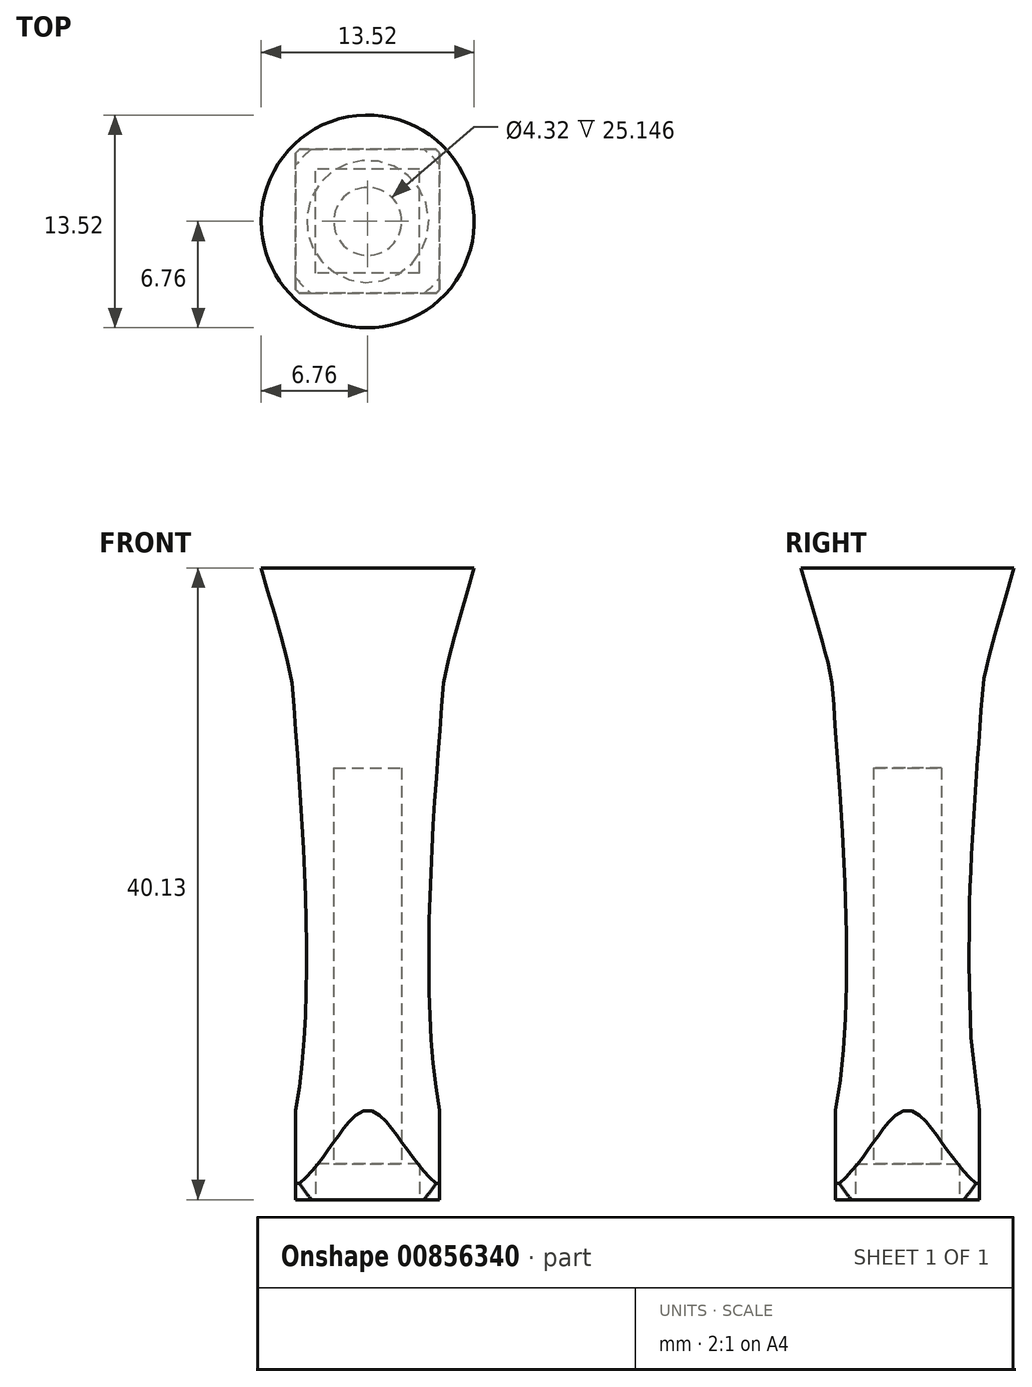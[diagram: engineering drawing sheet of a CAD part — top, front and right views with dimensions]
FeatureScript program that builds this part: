
annotation { "Feature Type Name" : "Feature", "Feature Type Description" : "" }
export const myFeature = defineFeature(function(context is Context, id is Id, definition is map)
    precondition{}
    {
        {
            var Q0;
            Q0=qCreatedBy(makeId("Front.planeOp"),FACE);
            var sketch = newSketch(context, id + "F0", { "sketchPlane" : qUnion([Q0])});
            skLineSegment(sketch, "E0", {"start": v(0, 0) * mm, "end": v(2.16, 0) * mm});
            skLineSegment(sketch, "E1", {"start": v(2.16, 0) * mm, "end": v(2.16, 25.4) * mm});
            skLineSegment(sketch, "E2", {"start": v(2.16, 25.4) * mm, "end": v(0, 25.4) * mm});
            skLineSegment(sketch, "E3", {"start": v(0, 25.4) * mm, "end": v(0, 38.1) * mm});
            skArc(sketch, "E4", {"start": v(0, 38.1) * mm, "mid": v(3.48, 38.26) * mm, "end": v(6.94, 38.74) * mm});
            skLineSegment(sketch, "E5", {"start": v(0, 0) * mm, "end": v(0, -2.03) * mm});
            skLineSegment(sketch, "E6", {"start": v(0, -2.03) * mm, "end": v(7.62, -2.03) * mm});
            skFitSpline(sketch, "E7", {"points": [v(7.62, -2.03) * mm, v(4.61, 28.24) * mm, v(6.94, 38.74) * mm], "startDerivative": vector(-26.12, 9.72) * mm, "endDerivative": vector(18.7, 66.57) * mm});
            skLineSegment(sketch, "E8", {"start": v(0, 38.1) * mm, "end": v(12.68, 38.1) * mm});
            skSolve(sketch);
        }
        {
            var Q0;
            Q0=makeQuery(id+"F0.imprint","IMPRINT",FACE,{"disambiguationData":[TD([[makeQuery(id+"F0.imprint","IMPRINT",EDGE,{"derivedFrom":sQuery(id+"F0.wireOp",EDGE,"E0")}),-1.0]])]});
            var Q1;
            Q1=sQuery(id+"F0.wireOp",EDGE,"E3");
            revolve(context, id + "F1", {"surfaceOperationType" : NewSurfaceOperationType.NEW, "entities" : qUnion([Q0]), "axis" : qUnion([Q1]), "revolveType" : RevolveType.FULL});
        }
        {
            var Q0;
            Q0=makeQuery(id+"F1.opRevolve","SWEPT_FACE",FACE,{"disambiguationData":[OSD([sQuery(id+"F0.wireOp",EDGE,"E6")])]});
            var sketch = newSketch(context, id + "F2", { "sketchPlane" : qUnion([Q0])});
            skLineSegment(sketch, "E9.bottom", {"start": v(3.3, 3.3) * mm, "end": v(-3.3, 3.3) * mm});
            skLineSegment(sketch, "E9.top", {"start": v(3.3, -3.3) * mm, "end": v(-3.3, -3.3) * mm});
            skLineSegment(sketch, "E9.left", {"start": v(3.3, 3.3) * mm, "end": v(3.3, -3.3) * mm});
            skLineSegment(sketch, "E9.right", {"start": v(-3.3, 3.3) * mm, "end": v(-3.3, -3.3) * mm});
            skPoint(sketch, "E9.middle", {"position": v(0, 0) * mm});
            skLineSegment(sketch, "E10.bottom", {"start": v(-4.57, 4.57) * mm, "end": v(4.57, 4.57) * mm});
            skLineSegment(sketch, "E10.top", {"start": v(-4.57, -4.57) * mm, "end": v(4.57, -4.57) * mm});
            skLineSegment(sketch, "E10.left", {"start": v(-4.57, 4.57) * mm, "end": v(-4.57, -4.57) * mm});
            skLineSegment(sketch, "E10.right", {"start": v(4.57, 4.57) * mm, "end": v(4.57, -4.57) * mm});
            skLineSegment(sketch, "E11.0", {"start": v(-8.26, 8.26) * mm, "end": v(8.26, 8.26) * mm});
            skLineSegment(sketch, "E11.1", {"start": v(-8.26, 8.26) * mm, "end": v(-8.26, -8.26) * mm});
            skLineSegment(sketch, "E11.2", {"start": v(-8.26, -8.26) * mm, "end": v(8.26, -8.26) * mm});
            skLineSegment(sketch, "E11.3", {"start": v(8.26, 8.26) * mm, "end": v(8.26, -8.26) * mm});
            skSolve(sketch);
        }
        {
            var Q0;
            Q0=makeQuery(id+"F2.imprint","IMPRINT",FACE,{"disambiguationData":[TD([[makeQuery(id+"F2.imprint","IMPRINT",EDGE,{"derivedFrom":sQuery(id+"F2.wireOp",EDGE,"E9.bottom")}),1.0]])]});
            extrude(context, id + "F3", {"entities" : qUnion([Q0]), "operationType" : NewBodyOperationType.REMOVE, "oppositeDirection" : true, "depth" : 2.3 * mm, "offsetDistance" : 25.4 * mm});
        }
        {
            var Q0;
            Q0=makeQuery(id+"F3.boolean.opBoolean","COPY",EDGE,{"derivedFrom":makeQuery(id+"F3.opExtrude","CAP_EDGE",EDGE,{"disambiguationData":[OSD([sQuery(id+"F2.wireOp",EDGE,"E9.left")])],"isStart":true})});
            var Q1;
            Q1=makeQuery(id+"F3.boolean.opBoolean","COPY",EDGE,{"derivedFrom":makeQuery(id+"F3.opExtrude","CAP_EDGE",EDGE,{"disambiguationData":[OSD([sQuery(id+"F2.wireOp",EDGE,"E9.bottom")])],"isStart":true})});
            var Q2;
            Q2=makeQuery(id+"F3.boolean.opBoolean","COPY",EDGE,{"derivedFrom":makeQuery(id+"F3.opExtrude","CAP_EDGE",EDGE,{"disambiguationData":[OSD([sQuery(id+"F2.wireOp",EDGE,"E9.top")])],"isStart":true})});
            var Q3;
            Q3=makeQuery(id+"F3.boolean.opBoolean","COPY",EDGE,{"derivedFrom":makeQuery(id+"F3.opExtrude","CAP_EDGE",EDGE,{"disambiguationData":[OSD([sQuery(id+"F2.wireOp",EDGE,"E9.right")])],"isStart":true})});
            var Q4;
            Q4=makeQuery(id+"F1.opRevolve","SWEPT_EDGE",EDGE,{"disambiguationData":[OSD([sQuery(id+"F0.wireOp",EDGE,"E6"),sQuery(id+"F0.wireOp",EDGE,"E7")])]});
            chamfer(context, id + "F4", {"entities" : qUnion([Q0, Q1, Q2, Q3, Q4]), "width" : 0.64 * mm, "tangentPropagation" : true});
        }
        {
            var Q0;
            Q0=makeQuery(id+"F2.imprint","IMPRINT",FACE,{"disambiguationData":[TD([[makeQuery(id+"F2.imprint","IMPRINT",EDGE,{"derivedFrom":sQuery(id+"F2.wireOp",EDGE,"E11.0")}),-1.0]])]});
            var Q1;
            Q1=makeQuery(id+"F2.imprint","IMPRINT",FACE,{"disambiguationData":[TD([[makeQuery(id+"F2.imprint","IMPRINT",EDGE,{"derivedFrom":sQuery(id+"F2.wireOp",EDGE,"E10.bottom")}),1.0]])]});
            extrude(context, id + "F5", {"entities" : qUnion([Q0, Q1]), "operationType" : NewBodyOperationType.REMOVE, "oppositeDirection" : true, "depth" : 25.4 * mm, "offsetDistance" : 25.4 * mm});
        }
    });
